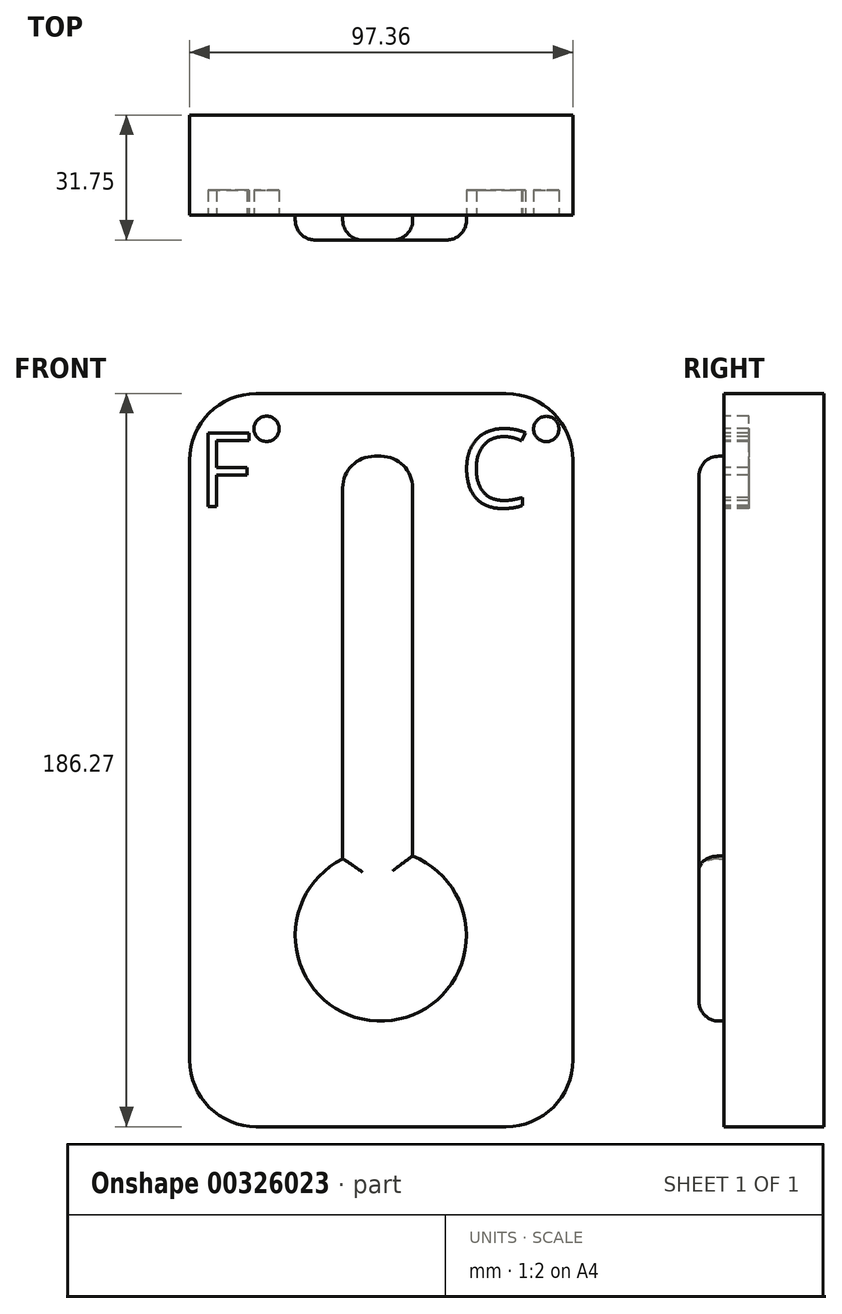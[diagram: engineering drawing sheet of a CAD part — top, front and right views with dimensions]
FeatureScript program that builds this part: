
annotation { "Feature Type Name" : "Feature", "Feature Type Description" : "" }
export const myFeature = defineFeature(function(context is Context, id is Id, definition is map)
    precondition{}
    {
        {
            var Q0;
            Q0=qCreatedBy(makeId("Front.planeOp"),FACE);
            var sketch = newSketch(context, id + "F0", { "sketchPlane" : qUnion([Q0])});
            skLineSegment(sketch, "E0.bottom", {"start": v(-31.65, 92.29) * mm, "end": v(31.85, 92.29) * mm});
            skLineSegment(sketch, "E0.top", {"start": v(-31.65, -93.98) * mm, "end": v(31.85, -93.98) * mm});
            skLineSegment(sketch, "E0.left", {"start": v(-48.58, 75.35) * mm, "end": v(-48.58, -77.05) * mm});
            skLineSegment(sketch, "E0.right", {"start": v(48.78, 75.35) * mm, "end": v(48.78, -77.05) * mm});
            skPoint(sketch, "E1.visualSharp", {"position": v(-48.58, 92.29) * mm});
            skArc(sketch, "E1.filletArc", {"start": v(-31.65, 92.29) * mm, "mid": v(-43.62, 87.33) * mm, "end": v(-48.58, 75.35) * mm});
            skPoint(sketch, "E2.visualSharp", {"position": v(48.78, 92.29) * mm});
            skArc(sketch, "E2.filletArc", {"start": v(48.78, 75.35) * mm, "mid": v(43.82, 87.33) * mm, "end": v(31.85, 92.29) * mm});
            skPoint(sketch, "E3.visualSharp", {"position": v(48.78, -93.98) * mm});
            skArc(sketch, "E3.filletArc", {"start": v(31.85, -93.98) * mm, "mid": v(43.82, -89.02) * mm, "end": v(48.78, -77.05) * mm});
            skPoint(sketch, "E4.visualSharp", {"position": v(-48.58, -93.98) * mm});
            skArc(sketch, "E4.filletArc", {"start": v(-48.58, -77.05) * mm, "mid": v(-43.62, -89.02) * mm, "end": v(-31.65, -93.98) * mm});
            skSolve(sketch);
        }
        {
            var Q0;
            Q0 = qSketchRegion(id + "F0", true);
            extrude(context, id + "F1", {"entities" : qUnion([Q0]), "depth" : 25.4 * mm});
        }
        {
            var Q0;
            Q0=makeQuery(id+"F1.opExtrude","CAP_FACE",FACE,{"disambiguationData":[OSD([sQuery(id+"F0.wireOp",EDGE,"E0.bottom"),sQuery(id+"F0.wireOp",EDGE,"E0.top"),sQuery(id+"F0.wireOp",EDGE,"E0.left"),sQuery(id+"F0.wireOp",EDGE,"E0.right"),sQuery(id+"F0.wireOp",EDGE,"E1.filletArc"),sQuery(id+"F0.wireOp",EDGE,"E2.filletArc"),sQuery(id+"F0.wireOp",EDGE,"E3.filletArc"),sQuery(id+"F0.wireOp",EDGE,"E4.filletArc")])],"isStart":false});
            var sketch = newSketch(context, id + "F2", { "sketchPlane" : qUnion([Q0])});
            skText(sketch, "E5", { "text": "F", "fontName": "OpenSans-Regular.ttf"});
            skText(sketch, "E6", { "text": "C", "fontName": "OpenSans-Regular.ttf"});
            skCircle(sketch, "E7", {"center": v(42.03, 83.3) * mm, "radius": 3.21 * mm});
            skCircle(sketch, "E8", {"center": v(-29.02, 83.32) * mm, "radius": 3.21 * mm});
            skLineSegment(sketch, "E9.bottom", {"start": v(-1.6, 76.36) * mm, "end": v(0, 76.36) * mm});
            skLineSegment(sketch, "E9.top", {"start": v(-9.68, -53.81) * mm, "end": v(8.09, -53.81) * mm});
            skLineSegment(sketch, "E9.left", {"start": v(-9.68, 68.28) * mm, "end": v(-9.68, -53.81) * mm});
            skLineSegment(sketch, "E9.right", {"start": v(8.09, 68.28) * mm, "end": v(8.09, -53.81) * mm});
            skPoint(sketch, "E10.visualSharp", {"position": v(-9.68, 76.36) * mm});
            skArc(sketch, "E10.filletArc", {"start": v(-1.6, 76.36) * mm, "mid": v(-7.32, 74) * mm, "end": v(-9.68, 68.28) * mm});
            skPoint(sketch, "E11.visualSharp", {"position": v(8.09, 76.36) * mm});
            skArc(sketch, "E11.filletArc", {"start": v(8.09, 68.28) * mm, "mid": v(5.72, 74) * mm, "end": v(0, 76.36) * mm});
            skCircle(sketch, "E12", {"center": v(0, -45.41) * mm, "radius": 21.75 * mm});
            const initialGuessF2  = {"E5": [-0.0464, 0.06363, 1, 0, 0.01874], "E6": [0.0201, 0.06334, 1, 0, 0.01995]};
            skSetInitialGuess(sketch, initialGuessF2);
            skSolve(sketch);
        }
        {
            var Q0;
            Q0 = qSketchRegion(id + "F2", true);
            extrude(context, id + "F3", {"entities" : qUnion([Q0]), "operationType" : NewBodyOperationType.REMOVE, "oppositeDirection" : true, "depth" : 6.35 * mm});
        }
        {
            var Q0;
            Q0=makeQuery(id+"F3.boolean.opBoolean","COPY",FACE,{"derivedFrom":makeQuery(id+"F3.opExtrude","CAP_FACE",FACE,{"disambiguationData":[OSD([sQuery(id+"F2.wireOp",EDGE,"E9.bottom"),sQuery(id+"F2.wireOp",EDGE,"E9.left"),sQuery(id+"F2.wireOp",EDGE,"E9.right"),sQuery(id+"F2.wireOp",EDGE,"E10.filletArc"),sQuery(id+"F2.wireOp",EDGE,"E11.filletArc"),sQuery(id+"F2.wireOp",EDGE,"E12")])],"isStart":false})});
            extrude(context, id + "F4", {"entities" : qUnion([Q0]), "operationType" : NewBodyOperationType.ADD, "depth" : 12.7 * mm});
        }
        {
            var Q0;
            Q0=makeQuery(id+"F4.opExtrude","CAP_EDGE",EDGE,{"disambiguationData":[OSD([sQuery(id+"F2.wireOp",EDGE,"E9.left")])],"isStart":false});
            var Q1;
            Q1=makeQuery(id+"F4.opExtrude","CAP_FACE",FACE,{"disambiguationData":[OSD([sQuery(id+"F2.wireOp",EDGE,"E9.bottom"),sQuery(id+"F2.wireOp",EDGE,"E9.left"),sQuery(id+"F2.wireOp",EDGE,"E9.right"),sQuery(id+"F2.wireOp",EDGE,"E10.filletArc"),sQuery(id+"F2.wireOp",EDGE,"E11.filletArc"),sQuery(id+"F2.wireOp",EDGE,"E12")])],"isStart":false});
            fillet(context, id + "F5", {"entities" : qUnion([Q0, Q1]), "radius" : 5.08 * mm, "tangentPropagation" : true, "allowEdgeOverflow" : false});
        }
    });
